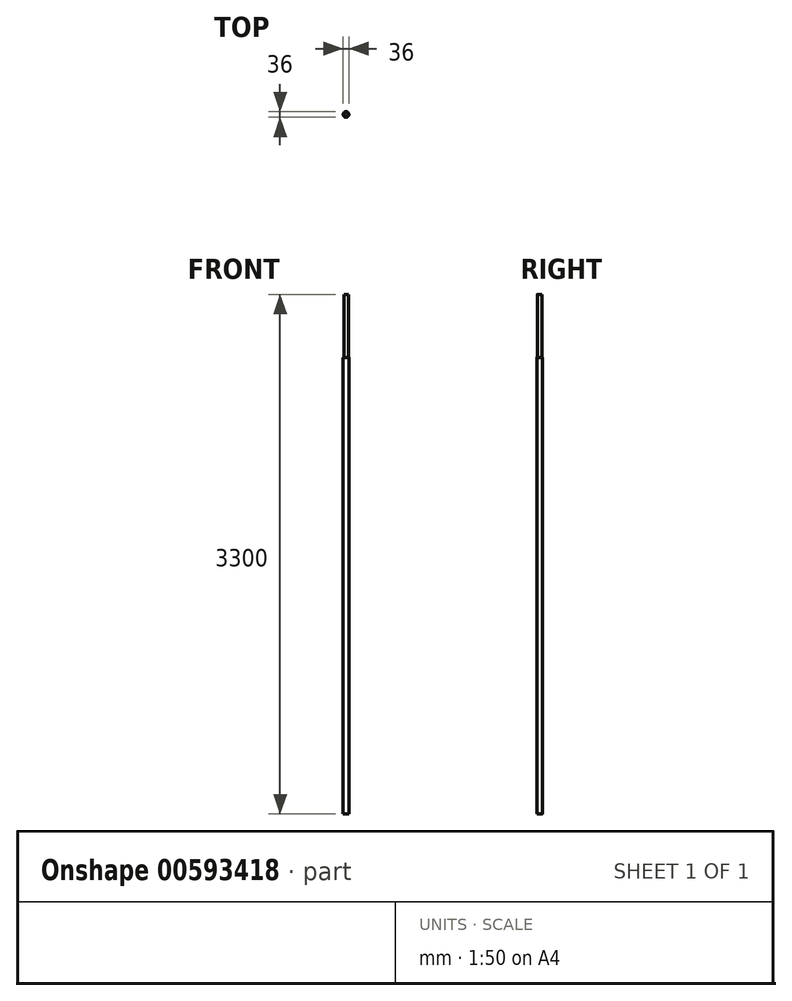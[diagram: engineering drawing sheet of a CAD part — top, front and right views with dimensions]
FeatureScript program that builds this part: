
annotation { "Feature Type Name" : "Feature", "Feature Type Description" : "" }
export const myFeature = defineFeature(function(context is Context, id is Id, definition is map)
    precondition{}
    {
        {
            var Q0;
            Q0=qCreatedBy(makeId("Front.planeOp"),FACE);
            var sketch = newSketch(context, id + "F0", { "sketchPlane" : qUnion([Q0])});
            skLineSegment(sketch, "E0", {"start": v(0, 3300) * mm, "end": v(0, 0) * mm});
            skLineSegment(sketch, "E1", {"start": v(0, 0) * mm, "end": v(-18, 0) * mm});
            skLineSegment(sketch, "E2", {"start": v(-18, 0) * mm, "end": v(-18, 2900) * mm});
            skLineSegment(sketch, "E3", {"start": v(-18, 2900) * mm, "end": v(-14, 2900) * mm});
            skLineSegment(sketch, "E4", {"start": v(-14, 2900) * mm, "end": v(-14, 3300) * mm});
            skLineSegment(sketch, "E5", {"start": v(-14, 3300) * mm, "end": v(0, 3300) * mm});
            skSolve(sketch);
        }
        {
            var Q0;
            Q0 = qSketchRegion(id + "F0", true);
            var Q1;
            Q1=sQuery(id+"F0.wireOp",EDGE,"E0");
            revolve(context, id + "F1", {"entities" : qUnion([Q0]), "axis" : qUnion([Q1]), "revolveType" : RevolveType.FULL});
        }
        {
            var Q0;
            Q0=makeQuery(id+"F1.opRevolve","SWEPT_FACE",FACE,{"disambiguationData":[OSD([sQuery(id+"F0.wireOp",EDGE,"E1")])]});
            var sketch = newSketch(context, id + "F2", { "sketchPlane" : qUnion([Q0])});
            skLineSegment(sketch, "E6.bottom", {"start": v(6, 6) * mm, "end": v(-6, 6) * mm});
            skLineSegment(sketch, "E6.top", {"start": v(6, -6) * mm, "end": v(-6, -6) * mm});
            skLineSegment(sketch, "E6.left", {"start": v(6, 6) * mm, "end": v(6, -6) * mm});
            skLineSegment(sketch, "E6.right", {"start": v(-6, 6) * mm, "end": v(-6, -6) * mm});
            skPoint(sketch, "E6.middle", {"position": v(0, 0) * mm});
            skSolve(sketch);
        }
        {
            var Q0;
            Q0 = qSketchRegion(id + "F2", true);
            extrude(context, id + "F3", {"entities" : qUnion([Q0]), "operationType" : NewBodyOperationType.REMOVE, "oppositeDirection" : true, "depth" : 4 * mm, "offsetDistance" : 25 * mm});
        }
    });
